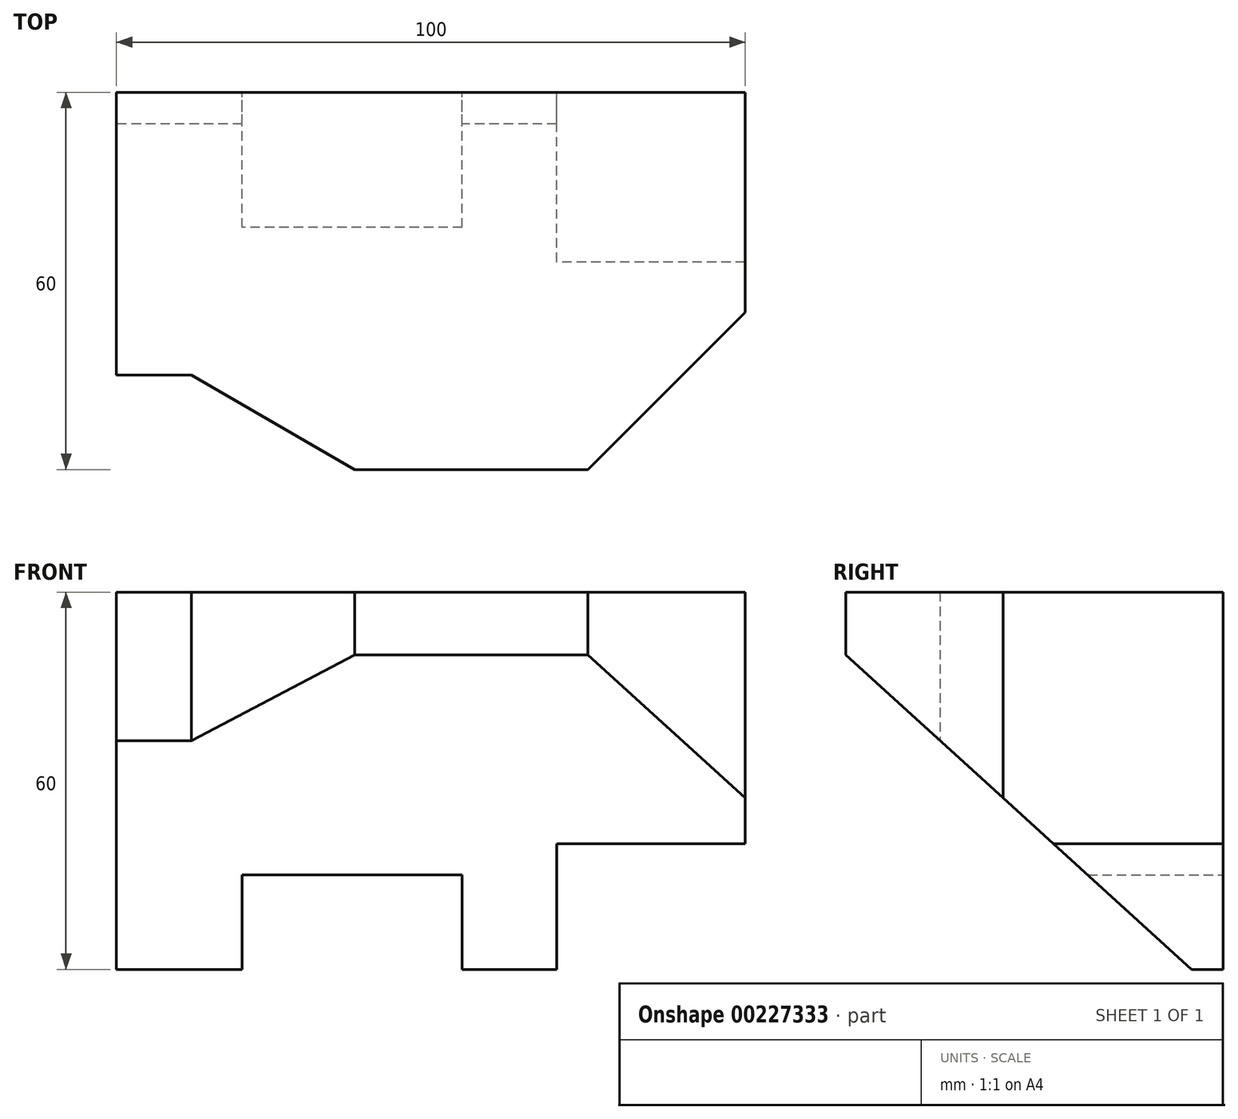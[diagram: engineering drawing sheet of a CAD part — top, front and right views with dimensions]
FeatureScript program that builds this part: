
annotation { "Feature Type Name" : "Feature", "Feature Type Description" : "" }
export const myFeature = defineFeature(function(context is Context, id is Id, definition is map)
    precondition{}
    {
        {
            var Q0;
            Q0=qCreatedBy(makeId("Front.planeOp"),FACE);
            var sketch = newSketch(context, id + "F0", { "sketchPlane" : qUnion([Q0])});
            skCircle(sketch, "E0", {"center": v(0, 0) * mm, "radius": 12 * mm});
            skCircle(sketch, "E1", {"center": v(40, 0) * mm, "radius": 5 * mm});
            skCircle(sketch, "E2", {"center": v(0, 0) * mm, "radius": 20 * mm});
            skArc(sketch, "E3", {"start": v(42.5, -9.68) * mm, "mid": v(50, 0) * mm, "end": v(42.5, 9.68) * mm});
            skLineSegment(sketch, "E4", {"start": v(5, 19.36) * mm, "end": v(42.5, 9.68) * mm});
            skLineSegment(sketch, "E5", {"start": v(5, -19.36) * mm, "end": v(42.5, -9.68) * mm});
            skSolve(sketch);
        }
        {
            var Q0;
            Q0=qCreatedBy(makeId("Front.planeOp"),FACE);
            var sketch = newSketch(context, id + "F1", { "sketchPlane" : qUnion([Q0])});
            skLineSegment(sketch, "E6.bottom", {"start": v(-40, 40) * mm, "end": v(-30, 40) * mm});
            skLineSegment(sketch, "E6.top", {"start": v(-40, 0) * mm, "end": v(40, 0) * mm});
            skLineSegment(sketch, "E6.left", {"start": v(-40, 40) * mm, "end": v(-40, 0) * mm});
            skLineSegment(sketch, "E6.right", {"start": v(40, 40) * mm, "end": v(40, 0) * mm});
            skArc(sketch, "E7", {"start": v(-30, 40) * mm, "mid": v(0, 10) * mm, "end": v(30, 40) * mm});
            skLineSegment(sketch, "E8.trimOffspring", {"start": v(30, 40) * mm, "end": v(40, 40) * mm});
            skLineSegment(sketch, "E9", {"start": v(0, 0) * mm, "end": v(0, 10) * mm});
            skLineSegment(sketch, "E10", {"start": v(-40, 25) * mm, "end": v(-25.98, 25) * mm});
            skCircle(sketch, "E11", {"center": v(-30, 10) * mm, "radius": 4.97 * mm});
            skCircle(sketch, "E12", {"center": v(30, 10) * mm, "radius": 4.97 * mm});
            skSolve(sketch);
        }
        {
            var Q0;
            Q0=qCreatedBy(makeId("Front.planeOp"),FACE);
            var sketch = newSketch(context, id + "F2", { "sketchPlane" : qUnion([Q0])});
            skLineSegment(sketch, "E13.bottom", {"start": v(-38.64, 38.3) * mm, "end": v(61.36, 38.3) * mm});
            skLineSegment(sketch, "E13.top", {"start": v(-38.64, -21.7) * mm, "end": v(-18.64, -21.7) * mm});
            skLineSegment(sketch, "E13.left", {"start": v(-38.64, 38.3) * mm, "end": v(-38.64, -21.7) * mm});
            skLineSegment(sketch, "E13.right", {"start": v(61.36, 38.3) * mm, "end": v(61.36, -1.7) * mm});
            skLineSegment(sketch, "E14.top", {"start": v(-18.64, -6.7) * mm, "end": v(16.36, -6.7) * mm});
            skLineSegment(sketch, "E14.left", {"start": v(-18.64, -21.7) * mm, "end": v(-18.64, -6.7) * mm});
            skLineSegment(sketch, "E14.right", {"start": v(16.36, -21.7) * mm, "end": v(16.36, -6.7) * mm});
            skLineSegment(sketch, "E15.top", {"start": v(31.36, -1.7) * mm, "end": v(61.36, -1.7) * mm});
            skLineSegment(sketch, "E15.left", {"start": v(31.36, -21.7) * mm, "end": v(31.36, -1.7) * mm});
            skLineSegment(sketch, "E16.trimOffspring", {"start": v(16.36, -21.7) * mm, "end": v(31.36, -21.7) * mm});
            skSolve(sketch);
        }
        {
            var Q0;
            Q0=makeQuery(id+"F2.imprint","IMPRINT",FACE,{"disambiguationData":[TD([[makeQuery(id+"F2.imprint","IMPRINT",EDGE,{"derivedFrom":sQuery(id+"F2.wireOp",EDGE,"E13.bottom")}),-1.0]])]});
            extrude(context, id + "F3", {"entities" : qUnion([Q0]), "depth" : 60 * mm});
        }
        {
            var Q0;
            Q0=makeQuery(id+"F3.opExtrude","SWEPT_FACE",FACE,{"disambiguationData":[OSD([sQuery(id+"F2.wireOp",EDGE,"E13.top")])]});
            var sketch = newSketch(context, id + "F4", { "sketchPlane" : qUnion([Q0])});
            skLineSegment(sketch, "E17.0.0", {"start": v(-38.64, 0) * mm, "end": v(-18.64, 0) * mm});
            skLineSegment(sketch, "E17.0.1", {"start": v(-18.64, 0) * mm, "end": v(-18.64, 60) * mm});
            skLineSegment(sketch, "E17.0.2", {"start": v(-18.64, 60) * mm, "end": v(-38.64, 60) * mm});
            skLineSegment(sketch, "E17.0.3", {"start": v(-38.64, 60) * mm, "end": v(-38.64, 0) * mm});
            skLineSegment(sketch, "E18.0.0", {"start": v(-18.64, 0) * mm, "end": v(16.36, 0) * mm});
            skLineSegment(sketch, "E18.0.1", {"start": v(16.36, 0) * mm, "end": v(16.36, 60) * mm});
            skLineSegment(sketch, "E18.0.2", {"start": v(16.36, 60) * mm, "end": v(-18.64, 60) * mm});
            skLineSegment(sketch, "E18.0.3", {"start": v(-18.64, 60) * mm, "end": v(-18.64, 0) * mm});
            skLineSegment(sketch, "E19.0.0", {"start": v(16.36, 0) * mm, "end": v(31.36, 0) * mm});
            skLineSegment(sketch, "E19.0.1", {"start": v(31.36, 0) * mm, "end": v(31.36, 60) * mm});
            skLineSegment(sketch, "E19.0.2", {"start": v(31.36, 60) * mm, "end": v(16.36, 60) * mm});
            skLineSegment(sketch, "E19.0.3", {"start": v(16.36, 60) * mm, "end": v(16.36, 0) * mm});
            skLineSegment(sketch, "E20.0.0", {"start": v(31.36, 0) * mm, "end": v(61.36, 0) * mm});
            skLineSegment(sketch, "E20.0.1", {"start": v(61.36, 0) * mm, "end": v(61.36, 60) * mm});
            skLineSegment(sketch, "E20.0.2", {"start": v(61.36, 60) * mm, "end": v(31.36, 60) * mm});
            skLineSegment(sketch, "E20.0.3", {"start": v(31.36, 60) * mm, "end": v(31.36, 0) * mm});
            skLineSegment(sketch, "E21.0.0", {"start": v(-38.64, 0) * mm, "end": v(-18.64, 0) * mm, "construction": true});
            skLineSegment(sketch, "E21.0.1", {"start": v(-18.64, 0) * mm, "end": v(-18.64, 60) * mm, "construction": true});
            skLineSegment(sketch, "E21.0.2", {"start": v(-18.64, 60) * mm, "end": v(-38.64, 60) * mm, "construction": true});
            skLineSegment(sketch, "E21.0.3", {"start": v(-38.64, 60) * mm, "end": v(-38.64, 0) * mm, "construction": true});
            skLineSegment(sketch, "E22.0.0", {"start": v(-18.64, 0) * mm, "end": v(16.36, 0) * mm, "construction": true});
            skLineSegment(sketch, "E22.0.1", {"start": v(16.36, 0) * mm, "end": v(16.36, 60) * mm, "construction": true});
            skLineSegment(sketch, "E22.0.2", {"start": v(16.36, 60) * mm, "end": v(-18.64, 60) * mm, "construction": true});
            skLineSegment(sketch, "E22.0.3", {"start": v(-18.64, 60) * mm, "end": v(-18.64, 0) * mm, "construction": true});
            skLineSegment(sketch, "E23.0.0", {"start": v(16.36, 0) * mm, "end": v(31.36, 0) * mm, "construction": true});
            skLineSegment(sketch, "E23.0.1", {"start": v(31.36, 0) * mm, "end": v(31.36, 60) * mm, "construction": true});
            skLineSegment(sketch, "E23.0.2", {"start": v(31.36, 60) * mm, "end": v(16.36, 60) * mm, "construction": true});
            skLineSegment(sketch, "E23.0.3", {"start": v(16.36, 60) * mm, "end": v(16.36, 0) * mm, "construction": true});
            skLineSegment(sketch, "E24.0.0", {"start": v(31.36, 0) * mm, "end": v(61.36, 0) * mm, "construction": true});
            skLineSegment(sketch, "E24.0.1", {"start": v(61.36, 0) * mm, "end": v(61.36, 60) * mm, "construction": true});
            skLineSegment(sketch, "E24.0.2", {"start": v(61.36, 60) * mm, "end": v(31.36, 60) * mm, "construction": true});
            skLineSegment(sketch, "E24.0.3", {"start": v(31.36, 60) * mm, "end": v(31.36, 0) * mm, "construction": true});
            skLineSegment(sketch, "E25", {"start": v(-0.73, 60) * mm, "end": v(-26.71, 45) * mm});
            skLineSegment(sketch, "E26", {"start": v(-26.71, 45) * mm, "end": v(-38.64, 45) * mm});
            skLineSegment(sketch, "E27", {"start": v(-38.64, 45) * mm, "end": v(-38.64, 60) * mm});
            skLineSegment(sketch, "E28", {"start": v(36.36, 60) * mm, "end": v(61.36, 35) * mm});
            skLineSegment(sketch, "E29", {"start": v(61.36, 35) * mm, "end": v(61.36, 60) * mm});
            skLineSegment(sketch, "E30", {"start": v(36.36, 60) * mm, "end": v(61.36, 60) * mm});
            skSolve(sketch);
        }
        {
            var Q0;
            {var subQ4=sQuery(id+"F4.wireOp",EDGE,"E17.0.2");Q0=makeQuery(id+"F4.imprint","IMPRINT",FACE,{"disambiguationData":[TD([[makeQuery(id+"F4.imprint","IMPRINT",EDGE,{"derivedFrom":subQ4}),-1.0]])]});}
            var Q1;
            {var subQ1=sQuery(id+"F4.wireOp",EDGE,"E18.0.2");var subQ3=sQuery(id+"F4.wireOp",EDGE,"E25");var subQ4=makeQuery(id+"F4.imprint","INTERSECT",VERTEX,{"derivedFrom":[subQ1,subQ3]});Q1=makeQuery(id+"F4.imprint","IMPRINT",FACE,{"disambiguationData":[TD([[makeQuery(id+"F4.imprint","IMPRINT",EDGE,{"disambiguationData":[TD([[subQ4,-1.0]])],"derivedFrom":subQ3}),-1.0]])]});}
            var Q2;
            Q2=makeQuery(id+"F4.imprint","IMPRINT",FACE,{"disambiguationData":[TD([[makeQuery(id+"F4.imprint","IMPRINT",EDGE,{"derivedFrom":sQuery(id+"F4.wireOp",EDGE,"E28")}),1.0]])]});
            extrude(context, id + "F5", {"entities" : qUnion([Q0, Q1, Q2]), "operationType" : NewBodyOperationType.REMOVE, "endBound" : BoundingType.THROUGH_ALL, "oppositeDirection" : true, "depth" : 25 * mm});
        }
        {
            var Q0;
            Q0=makeQuery(id+"F3.opExtrude","SWEPT_FACE",FACE,{"disambiguationData":[OSD([sQuery(id+"F2.wireOp",EDGE,"E13.left")])]});
            var sketch = newSketch(context, id + "F6", { "sketchPlane" : qUnion([Q0])});
            skLineSegment(sketch, "E31.0.0", {"start": v(49.66, -21.7) * mm, "end": v(49.66, -6.7) * mm, "construction": true});
            skLineSegment(sketch, "E31.0.1", {"start": v(49.66, -6.7) * mm, "end": v(60, -6.7) * mm, "construction": true});
            skLineSegment(sketch, "E31.0.2", {"start": v(60, -6.7) * mm, "end": v(60, 38.3) * mm, "construction": true});
            skLineSegment(sketch, "E31.0.3", {"start": v(60, 38.3) * mm, "end": v(45, 38.3) * mm, "construction": true});
            skLineSegment(sketch, "E31.0.4", {"start": v(45, 38.3) * mm, "end": v(45, -21.7) * mm, "construction": true});
            skLineSegment(sketch, "E31.0.5", {"start": v(45, -21.7) * mm, "end": v(49.66, -21.7) * mm, "construction": true});
            skLineSegment(sketch, "E32.0.0", {"start": v(45, -21.7) * mm, "end": v(45, 38.3) * mm, "construction": true});
            skLineSegment(sketch, "E32.0.1", {"start": v(45, 38.3) * mm, "end": v(0, 38.3) * mm, "construction": true});
            skLineSegment(sketch, "E32.0.2", {"start": v(0, 38.3) * mm, "end": v(0, -21.7) * mm, "construction": true});
            skLineSegment(sketch, "E32.0.3", {"start": v(0, -21.7) * mm, "end": v(45, -21.7) * mm, "construction": true});
            skLineSegment(sketch, "E33", {"start": v(60, 28.3) * mm, "end": v(5, -21.7) * mm});
            skLineSegment(sketch, "E34", {"start": v(5, -21.7) * mm, "end": v(60, -21.7) * mm});
            skLineSegment(sketch, "E35", {"start": v(60, -21.7) * mm, "end": v(60, 28.3) * mm});
            skSolve(sketch);
        }
        {
            var Q0;
            {var subQ0=sQuery(id+"F6.wireOp",EDGE,"E35");Q0=makeQuery(id+"F6.imprint","IMPRINT",FACE,{"disambiguationData":[TD([[makeQuery(id+"F6.imprint","IMPRINT",EDGE,{"derivedFrom":subQ0}),1.0]])]});}
            var Q1;
            {var subQ0=sQuery(id+"F6.wireOp",EDGE,"E34");var subQ1=sQuery(id+"F6.wireOp",EDGE,"E33");var subQ2=makeQuery(id+"F6.imprint","INTERSECT",VERTEX,{"derivedFrom":[makeQuery(id+"F3.opExtrude","SWEPT_EDGE",EDGE,{"disambiguationData":[OSD([sQuery(id+"F2.wireOp",EDGE,"E13.top"),sQuery(id+"F2.wireOp",EDGE,"E13.left")])]}),subQ1,subQ0]});Q1=makeQuery(id+"F6.imprint","IMPRINT",FACE,{"disambiguationData":[TD([[makeQuery(id+"F6.imprint","IMPRINT",EDGE,{"disambiguationData":[TD([[subQ2,1.0]])],"derivedFrom":subQ1}),1.0]])]});}
            extrude(context, id + "F7", {"entities" : qUnion([Q0, Q1]), "operationType" : NewBodyOperationType.REMOVE, "endBound" : BoundingType.THROUGH_ALL, "oppositeDirection" : true, "depth" : 25 * mm});
        }
    });
